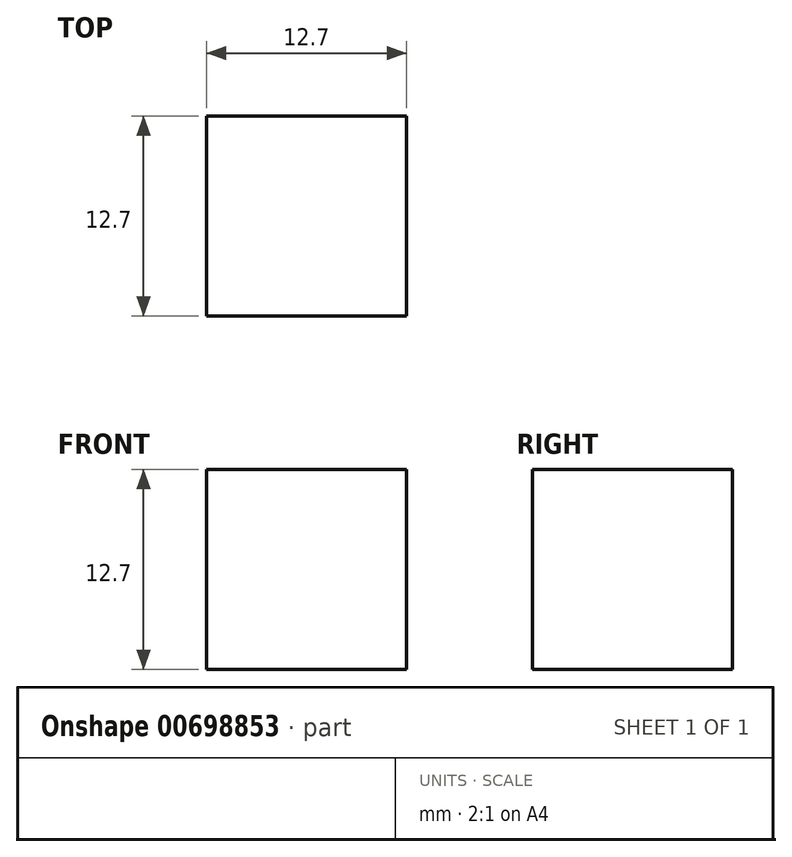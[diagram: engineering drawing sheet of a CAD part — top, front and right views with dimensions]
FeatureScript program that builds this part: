
annotation { "Feature Type Name" : "Feature", "Feature Type Description" : "" }
export const myFeature = defineFeature(function(context is Context, id is Id, definition is map)
    precondition{}
    {
        {
            var Q0;
            Q0=qCreatedBy(makeId("Top.planeOp"),FACE);
            var sketch = newSketch(context, id + "F0", { "sketchPlane" : qUnion([Q0])});
            skLineSegment(sketch, "E0.bottom", {"start": v(0, 0) * mm, "end": v(-12.7, 0) * mm});
            skLineSegment(sketch, "E0.top", {"start": v(0, 12.7) * mm, "end": v(-12.7, 12.7) * mm});
            skLineSegment(sketch, "E0.left", {"start": v(0, 0) * mm, "end": v(0, 12.7) * mm});
            skLineSegment(sketch, "E0.right", {"start": v(-12.7, 0) * mm, "end": v(-12.7, 12.7) * mm});
            skSolve(sketch);
        }
        {
            var Q0;
            Q0=makeQuery(id+"F0.imprint","IMPRINT",FACE,{"disambiguationData":[TD([[makeQuery(id+"F0.imprint","IMPRINT",EDGE,{"derivedFrom":sQuery(id+"F0.wireOp",EDGE,"E0.bottom")}),-1.0]])]});
            extrude(context, id + "F1", {"entities" : qUnion([Q0]), "depth" : 12.7 * mm, "offsetDistance" : 25.4 * mm});
        }
    });
